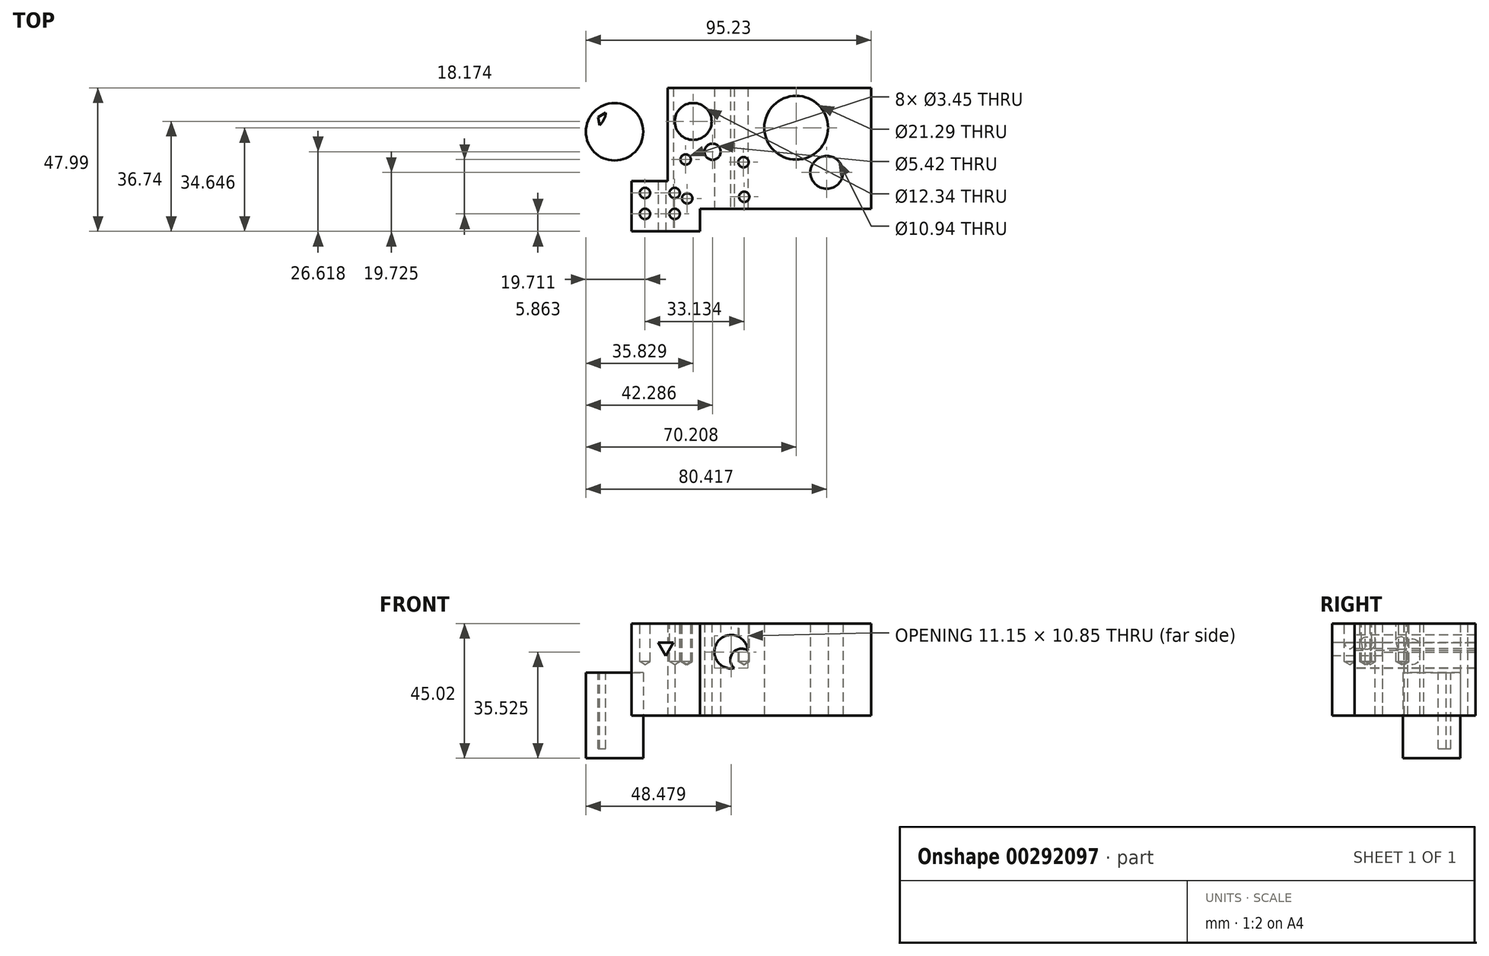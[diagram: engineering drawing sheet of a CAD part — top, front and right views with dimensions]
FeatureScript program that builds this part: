
annotation { "Feature Type Name" : "Feature", "Feature Type Description" : "" }
export const myFeature = defineFeature(function(context is Context, id is Id, definition is map)
    precondition{}
    {
        {
            var Q0;
            Q0=qCreatedBy(makeId("Top.planeOp"),FACE);
            var sketch = newSketch(context, id + "F0", { "sketchPlane" : qUnion([Q0])});
            skLineSegment(sketch, "E0.bottom", {"start": v(-38.55, 26.17) * mm, "end": v(29.43, 26.17) * mm});
            skLineSegment(sketch, "E0.top", {"start": v(-27.73, -14.26) * mm, "end": v(29.43, -14.26) * mm});
            skLineSegment(sketch, "E0.left", {"start": v(-38.55, 26.17) * mm, "end": v(-38.55, -5) * mm});
            skLineSegment(sketch, "E0.right", {"start": v(29.43, 26.17) * mm, "end": v(29.43, -14.26) * mm});
            skCircle(sketch, "E1", {"center": v(-29.97, 14.92) * mm, "radius": 6.17 * mm});
            skCircle(sketch, "E2", {"center": v(-23.51, 4.8) * mm, "radius": 2.7 * mm});
            skCircle(sketch, "E3", {"center": v(4.4, 12.83) * mm, "radius": 10.65 * mm});
            skCircle(sketch, "E4", {"center": v(14.62, -2.1) * mm, "radius": 5.47 * mm});
            skLineSegment(sketch, "E5.bottom", {"start": v(-50.62, -5) * mm, "end": v(-38.55, -5) * mm});
            skLineSegment(sketch, "E5.top", {"start": v(-50.62, -21.82) * mm, "end": v(-27.73, -21.82) * mm});
            skLineSegment(sketch, "E5.left", {"start": v(-50.62, -5) * mm, "end": v(-50.62, -21.82) * mm});
            skLineSegment(sketch, "E5.right", {"start": v(-27.73, -14.26) * mm, "end": v(-27.73, -21.82) * mm});
            skSolve(sketch);
        }
        {
            var Q0;
            Q0 = qSketchRegion(id + "F0", true);
            extrude(context, id + "F1", {"entities" : qUnion([Q0]), "depth" : 30.73 * mm});
        }
        {
            var Q0;
            Q0=makeQuery(id+"F1.opExtrude","SWEPT_FACE",FACE,{"disambiguationData":[OSD([sQuery(id+"F0.wireOp",EDGE,"E5.top")])]});
            var sketch = newSketch(context, id + "F2", { "sketchPlane" : qUnion([Q0])});
            skCircle(sketch, "E6.cCircle", {"center": v(-39.17, 22.92) * mm, "radius": 1.47 * mm, "construction": true});
            skLineSegment(sketch, "E6.0", {"start": v(-36.63, 24.38) * mm, "end": v(-39.17, 19.98) * mm});
            skLineSegment(sketch, "E6.1", {"start": v(-39.17, 19.98) * mm, "end": v(-41.71, 24.38) * mm});
            skLineSegment(sketch, "E6.2", {"start": v(-41.71, 24.38) * mm, "end": v(-36.63, 24.38) * mm});
            skPoint(sketch, "E6.0.midPoint", {"position": v(-37.9, 22.18) * mm});
            skLineSegment(sketch, "E7", {"start": v(-50.62, 22.92) * mm, "end": v(-27.73, 22.92) * mm, "construction": true});
            skSolve(sketch);
        }
        {
            var Q0;
            Q0=makeQuery(id+"F2.imprint","IMPRINT",FACE,{"disambiguationData":[TD([[makeQuery(id+"F2.imprint","IMPRINT",EDGE,{"derivedFrom":sQuery(id+"F2.wireOp",EDGE,"E6.0")}),-1.0]])]});
            extrude(context, id + "F3", {"entities" : qUnion([Q0]), "operationType" : NewBodyOperationType.REMOVE, "endBound" : BoundingType.THROUGH_ALL, "oppositeDirection" : true, "depth" : 48.64 * mm});
        }
        {
            var Q0;
            Q0=makeQuery(id+"F1.opExtrude","SWEPT_FACE",FACE,{"disambiguationData":[OSD([sQuery(id+"F0.wireOp",EDGE,"E0.top")])]});
            var sketch = newSketch(context, id + "F4", { "sketchPlane" : qUnion([Q0])});
            skCircle(sketch, "E8", {"center": v(-17.32, 21.3) * mm, "radius": 5.59 * mm});
            skCircle(sketch, "E9", {"center": v(-13.84, 18.6) * mm, "radius": 3.74 * mm});
            skCircle(sketch, "E10", {"center": v(-12.4, 17.4) * mm, "radius": 2.9 * mm});
            skCircle(sketch, "E11", {"center": v(-11.56, 16.39) * mm, "radius": 2.34 * mm});
            skCircle(sketch, "E12", {"center": v(-10.72, 15.73) * mm, "radius": 1.66 * mm});
            skSolve(sketch);
        }
        {
            var Q0;
            {var subQ0=sQuery(id+"F4.wireOp",EDGE,"E9");var subQ1=sQuery(id+"F4.wireOp",EDGE,"E8");var subQ2=makeQuery(id+"F4.imprint","INTERSECT",VERTEX,{"disambiguationData":[OD(0.0)],"derivedFrom":[subQ1,subQ0]});Q0=makeQuery(id+"F4.imprint","IMPRINT",FACE,{"disambiguationData":[TD([[makeQuery(id+"F4.imprint","IMPRINT",EDGE,{"disambiguationData":[TD([[subQ2,1.0]])],"derivedFrom":subQ1}),1.0]])]});}
            var Q1;
            Q1=sQuery(id+"F4.wireOp",EDGE,"E12");
            var Q2;
            Q2=sQuery(id+"F4.wireOp",EDGE,"E8");
            var Q3;
            Q3=sQuery(id+"F4.wireOp",EDGE,"E9");
            var Q4;
            Q4=sQuery(id+"F4.wireOp",EDGE,"E11");
            var Q5;
            Q5=sQuery(id+"F4.wireOp",EDGE,"E10");
            extrude(context, id + "F5", {"entities" : qUnion([Q0]), "operationType" : NewBodyOperationType.REMOVE, "surfaceEntities" : qUnion([Q1, Q2, Q3, Q4, Q5]), "endBound" : BoundingType.THROUGH_ALL, "oppositeDirection" : true, "depth" : 25.4 * mm});
        }
        {
            var Q0;
            Q0=qCreatedBy(makeId("Top.planeOp"),FACE);
            var sketch = newSketch(context, id + "F6", { "sketchPlane" : qUnion([Q0])});
            skCircle(sketch, "E13", {"center": v(-56.22, 11.48) * mm, "radius": 9.58 * mm});
            skSolve(sketch);
        }
        {
            var Q0;
            Q0 = qSketchRegion(id + "F6", true);
            extrude(context, id + "F7", {"entities" : qUnion([Q0]), "endBound" : BoundingType.SYMMETRIC, "depth" : 28.57 * mm});
        }
        {
            var Q0;
            Q0=makeQuery(id+"F7.opExtrude","CAP_FACE",FACE,{"disambiguationData":[OSD([sQuery(id+"F6.wireOp",EDGE,"E13")])],"isStart":false});
            var sketch = newSketch(context, id + "F8", { "sketchPlane" : qUnion([Q0])});
            skLineSegment(sketch, "E14", {"start": v(-78.42, 3.8) * mm, "end": v(-62.73, -1.13) * mm});
            skLineSegment(sketch, "E15", {"start": v(-61.1, 12.35) * mm, "end": v(-64.95, 14.48) * mm});
            skLineSegment(sketch, "E16", {"start": v(-74.05, 9.22) * mm, "end": v(-59.12, 17.85) * mm});
            skLineSegment(sketch, "E17", {"start": v(-60.39, 7.51) * mm, "end": v(-63, 25.3) * mm});
            skPoint(sketch, "E17.endSnap0", {"position": v(-62.46, 13.1) * mm});
            skArc(sketch, "E18", {"start": v(-62.24, 12.98) * mm, "mid": v(-60.09, 15.02) * mm, "end": v(-59.16, 17.83) * mm});
            skPoint(sketch, "E19.orphan", {"position": v(-88.21, 27.34) * mm});
            skPoint(sketch, "E20.orphan", {"position": v(-62.46, 21.66) * mm});
            skPoint(sketch, "E21.orphan", {"position": v(-36.71, -1.13) * mm});
            skLineSegment(sketch, "E22", {"start": v(-75.98, 8.1) * mm, "end": v(-69.11, 1.84) * mm});
            skLineSegment(sketch, "E23", {"start": v(-69.11, 1.84) * mm, "end": v(-59.84, 3.79) * mm});
            skSolve(sketch);
        }
        {
            var Q0;
            {var subQ0=sQuery(id+"F8.wireOp",EDGE,"E18");var subQ1=sQuery(id+"F8.wireOp",EDGE,"E16");var subQ2=makeQuery(id+"F8.imprint","INTERSECT",VERTEX,{"derivedFrom":[subQ1,subQ0]});Q0=makeQuery(id+"F8.imprint","IMPRINT",FACE,{"disambiguationData":[TD([[makeQuery(id+"F8.imprint","IMPRINT",EDGE,{"disambiguationData":[TD([[subQ2,1.0]])],"derivedFrom":subQ1}),-1.0]])]});}
            extrude(context, id + "F9", {"entities" : qUnion([Q0]), "operationType" : NewBodyOperationType.REMOVE, "oppositeDirection" : true, "depth" : 25.4 * mm});
        }
        {
            var Q0;
            Q0=makeQuery(id+"F1.opExtrude","CAP_FACE",FACE,{"disambiguationData":[OSD([sQuery(id+"F0.wireOp",EDGE,"E0.bottom"),sQuery(id+"F0.wireOp",EDGE,"E0.top"),sQuery(id+"F0.wireOp",EDGE,"E0.left"),sQuery(id+"F0.wireOp",EDGE,"E0.right"),sQuery(id+"F0.wireOp",EDGE,"E1"),sQuery(id+"F0.wireOp",EDGE,"E2"),sQuery(id+"F0.wireOp",EDGE,"E3"),sQuery(id+"F0.wireOp",EDGE,"E4"),sQuery(id+"F0.wireOp",EDGE,"E5.bottom"),sQuery(id+"F0.wireOp",EDGE,"E5.top"),sQuery(id+"F0.wireOp",EDGE,"E5.left"),sQuery(id+"F0.wireOp",EDGE,"E5.right")])],"isStart":false});
            var sketch = newSketch(context, id + "F10", { "sketchPlane" : qUnion([Q0])});
            skPoint(sketch, "E24", {"position": v(-32.5, 2.22) * mm});
            skPoint(sketch, "E25", {"position": v(-31.98, -10.79) * mm});
            skPoint(sketch, "E26", {"position": v(-12.95, -10.24) * mm});
            skPoint(sketch, "E27", {"position": v(-13.19, 1.3) * mm});
            skLineSegment(sketch, "E28.bottom", {"start": v(-46.09, -9) * mm, "end": v(-36.17, -9) * mm});
            skLineSegment(sketch, "E28.top", {"start": v(-46.09, -15.96) * mm, "end": v(-36.17, -15.96) * mm});
            skLineSegment(sketch, "E28.left", {"start": v(-46.09, -9) * mm, "end": v(-46.09, -15.96) * mm});
            skLineSegment(sketch, "E28.right", {"start": v(-36.17, -9) * mm, "end": v(-36.17, -15.96) * mm});
            skSolve(sketch);
        }
        {
            var Q0;
            Q0=sQuery(id+"F10.wireOp",VERTEX,"E28.left.start");
            var Q1;
            Q1=sQuery(id+"F10.wireOp",VERTEX,"E28.left.end");
            var Q2;
            Q2=sQuery(id+"F10.wireOp",VERTEX,"E28.right.start");
            var Q3;
            Q3=sQuery(id+"F10.wireOp",VERTEX,"E28.right.end");
            var Q4;
            Q4=sQuery(id+"F10.wireOp",VERTEX,"E25");
            var Q5;
            Q5=sQuery(id+"F10.wireOp",VERTEX,"E24");
            var Q6;
            Q6=sQuery(id+"F10.wireOp",VERTEX,"E27");
            var Q7;
            Q7=sQuery(id+"F10.wireOp",VERTEX,"E26");
            var Q8;
            Q8=makeQuery(id+"F1.opExtrude","SWEPT_BODY",BODY,{"disambiguationData":[OSD([sQuery(id+"F0.wireOp",EDGE,"E0.bottom"),sQuery(id+"F0.wireOp",EDGE,"E0.top"),sQuery(id+"F0.wireOp",EDGE,"E0.left"),sQuery(id+"F0.wireOp",EDGE,"E0.right"),sQuery(id+"F0.wireOp",EDGE,"E1"),sQuery(id+"F0.wireOp",EDGE,"E2"),sQuery(id+"F0.wireOp",EDGE,"E3"),sQuery(id+"F0.wireOp",EDGE,"E4"),sQuery(id+"F0.wireOp",EDGE,"E5.bottom"),sQuery(id+"F0.wireOp",EDGE,"E5.top"),sQuery(id+"F0.wireOp",EDGE,"E5.left"),sQuery(id+"F0.wireOp",EDGE,"E5.right")])]});
            hole(context, id + "F11", {"style" : HoleStyle.SIMPLE, "endStyle" : HoleEndStyle.BLIND, "standardTappedOrClearance" : lookupTablePath({ "standard" : "ANSI", "fit" : "Normal (ASME)", "size" : "#5", "type" : "Clearance" }), "standardBlindInLast" : lookupTablePath({ "fit" : "Free", "standard" : "ANSI", "size" : "#5", "type" : "Clearance" }), "holeDiameter" : 3.45 * mm, "holeDepth" : 12.7 * mm, "tappedDepth" : 12.7 * mm, "tapClearance" : 3, "locations" : qUnion([Q0, Q1, Q2, Q3, Q4, Q5, Q6, Q7]), "scope" : qUnion([Q8])});
        }
    });
